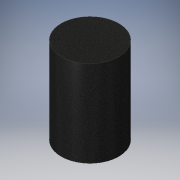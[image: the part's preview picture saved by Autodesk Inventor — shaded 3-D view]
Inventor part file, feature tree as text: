
AUTODESK INVENTOR PART (.ipt)
format: ipt  version: 2019.3 (Build 233278000, 278)  size: 105,472 bytes
history: native  units: mm
features: other x1, extrude x1, sketch x1
ambient origin geometry x8: Origin, YZ Plane, XZ Plane, XY Plane, X Axis, Y Axis, Z Axis, Center Point
bodies: Body1 (feature_tree)
feature tree (3):
  other  "ソリッド1"
  extrude  "押し出し1"  Depth=100.0mm
  sketch  "スケッチ1"
